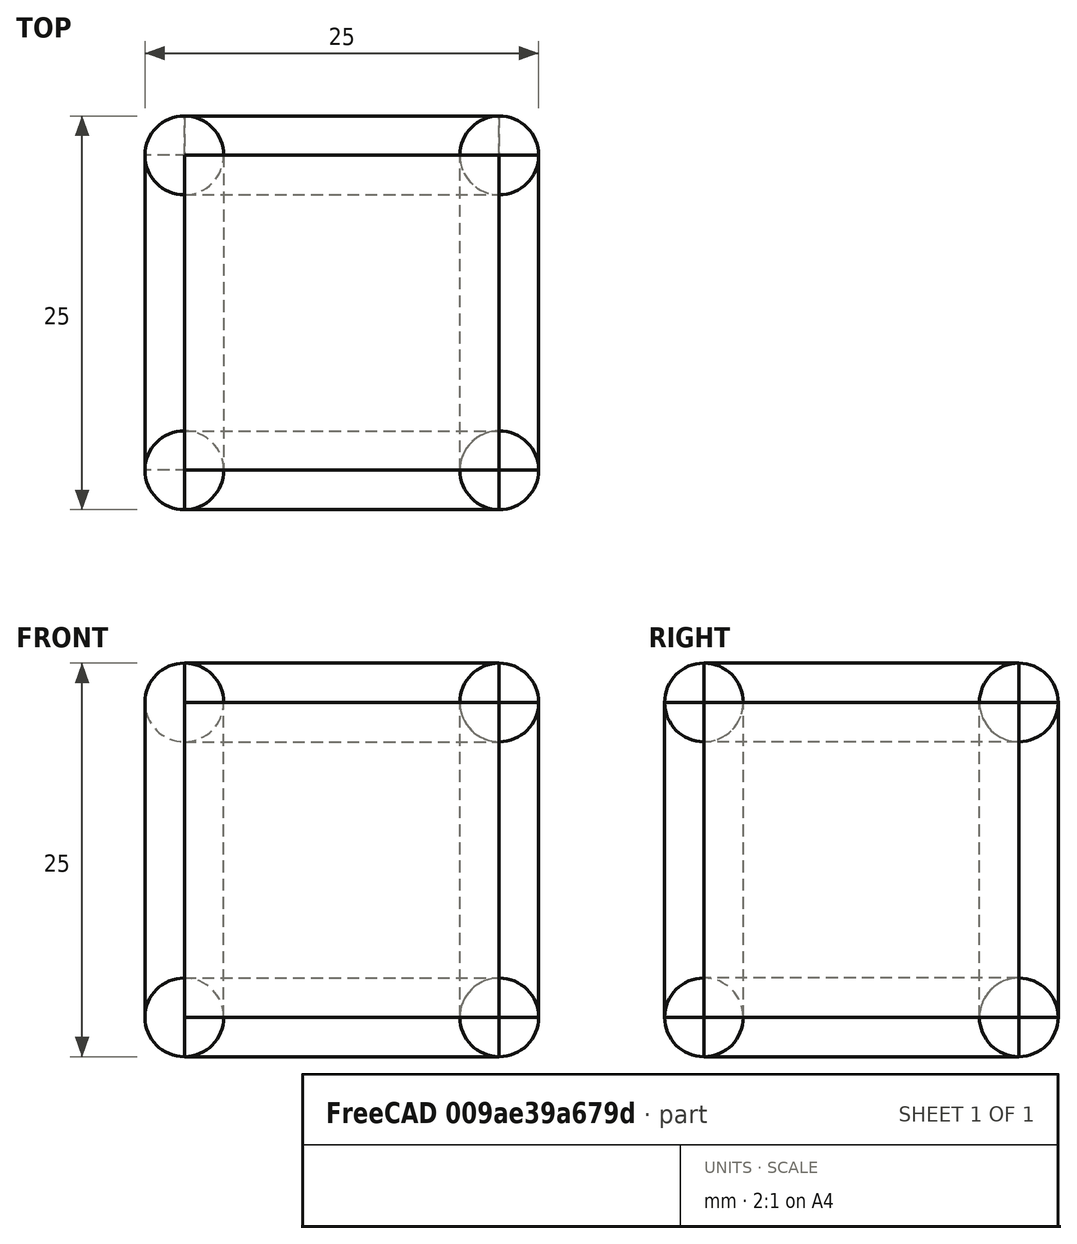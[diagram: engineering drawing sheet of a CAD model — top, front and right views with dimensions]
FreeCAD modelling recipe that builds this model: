
FCSTD DOCUMENT  (FreeCAD 0.16R6706 (Git))
Label: bricks
License: All rights reserved
LicenseURL: http://en.wikipedia.org/wiki/All_rights_reserved
objects: Part::FeaturePython×23, Part::Fuse×2, Part::Part2DObjectPython×2, Part::Sphere×1, Part::Cylinder×1, Part::Box×1, Drawing::FeatureViewPython×1, Drawing::FeaturePage×1
note: 30 computed .brp shape members not serialized (recipe doc carries the construction recipe); baked Part::Feature solids carry a one-line shape summary decoded from their .brp

FEATURE [Part::Sphere] Sphere
  Angle1 = -90
  Angle2 = 90
  Angle3 = 360
  Radius = 2.5
FEATURE [Part::FeaturePython] Clone  label="Clone of Sphere"  # Draft clone (typed FeaturePython)
  Objects = -> [Sphere]
  Placement = pos=(20,0,0) rot=(0,0,1;0rad)
  Scale = (1,1,1)
FEATURE [Part::FeaturePython] Clone001  label="Clone of Sphere001"  # Draft clone (typed FeaturePython)
  Objects = -> [Sphere]
  Placement = pos=(0,20,0) rot=(0,0,1;0rad)
  Scale = (1,1,1)
FEATURE [Part::FeaturePython] Clone002  label="Clone of Sphere002"  # Draft clone (typed FeaturePython)
  Objects = -> [Sphere]
  Placement = pos=(20,20,0) rot=(0,0,1;0rad)
  Scale = (1,1,1)
FEATURE [Part::FeaturePython] Clone003  label="Clone of Clone of Sphere002"  # Draft clone (typed FeaturePython)
  Objects = -> [Clone002]
  Placement = pos=(0,0,20) rot=(0,0,1;0rad)
  Scale = (1,1,1)
FEATURE [Part::FeaturePython] Clone005  label="Clone of Clone of Sphere"  # Draft clone (typed FeaturePython)
  Objects = -> [Clone]
  Placement = pos=(20,0,20) rot=(0,0,1;0rad)
  Scale = (1,1,1)
FEATURE [Part::FeaturePython] Clone004  label="Clone of Clone of Sphere001"  # Draft clone (typed FeaturePython)
  Objects = -> [Clone001]
  Placement = pos=(0,20,20) rot=(0,0,1;0rad)
  Scale = (1,1,1)
FEATURE [Part::FeaturePython] Clone006  label="Clone of Sphere003"  # Draft clone (typed FeaturePython)
  Objects = -> [Sphere]
  Placement = pos=(20,20,20) rot=(0,0,1;0rad)
  Scale = (1,1,1)
FEATURE [Part::Cylinder] Cylinder
  Angle = 360
  Height = 20
  Placement = pos=(0,20,0) rot=(0,0,1;0rad)
  Radius = 2.5
FEATURE [Part::FeaturePython] Clone007  label="Clone of Cylinder"  # Draft clone (typed FeaturePython)
  Objects = -> [Cylinder]
  Scale = (1,1,1)
FEATURE [Part::FeaturePython] Clone008  label="Clone of Cylinder001"  # Draft clone (typed FeaturePython)
  Objects = -> [Cylinder]
  Placement = pos=(20,20,0) rot=(0,0,1;0rad)
  Scale = (1,1,1)
FEATURE [Part::FeaturePython] Clone009  label="Clone of Cylinder002"  # Draft clone (typed FeaturePython)
  Objects = -> [Cylinder]
  Placement = pos=(20,0,0) rot=(0,0,1;0rad)
  Scale = (1,1,1)
FEATURE [Part::FeaturePython] Clone010  label="Clone of Cylinder003"  # Draft clone (typed FeaturePython)
  Objects = -> [Cylinder]
  Placement = pos=(0,20,20) rot=(0,1,0;1.5708rad)
  Scale = (1,1,1)
FEATURE [Part::FeaturePython] Clone011  label="Clone of Clone of Cylinder003"  # Draft clone (typed FeaturePython)
  Objects = -> [Clone010]
  Placement = pos=(0,0,0) rot=(0,1,0;1.5708rad)
  Scale = (1,1,1)
FEATURE [Part::FeaturePython] Clone012  label="Clone of Clone of Cylinder004"  # Draft clone (typed FeaturePython)
  Objects = -> [Clone010]
  Placement = pos=(0,20,0) rot=(0,1,0;1.5708rad)
  Scale = (1,1,1)
FEATURE [Part::FeaturePython] Clone013  label="Clone of Clone of Cylinder005"  # Draft clone (typed FeaturePython)
  Objects = -> [Clone010]
  Placement = pos=(0,0,20) rot=(0,1,0;1.5708rad)
  Scale = (1,1,1)
FEATURE [Part::FeaturePython] Clone014  label="Clone of Cylinder004"  # Draft clone (typed FeaturePython)
  Objects = -> [Cylinder]
  Placement = pos=(0,20,20) rot=(1,0,0;1.5708rad)
  Scale = (1,1,1)
FEATURE [Part::FeaturePython] Clone015  label="Clone of Clone of Cylinder006"  # Draft clone (typed FeaturePython)
  Objects = -> [Clone014]
  Placement = pos=(20,20,0) rot=(1,0,0;1.5708rad)
  Scale = (1,1,1)
FEATURE [Part::FeaturePython] Clone016  label="Clone of Clone of Cylinder007"  # Draft clone (typed FeaturePython)
  Objects = -> [Clone014]
  Placement = pos=(0,20,0) rot=(1,0,0;1.5708rad)
  Scale = (1,1,1)
FEATURE [Part::FeaturePython] Clone017  label="Clone of Clone of Cylinder008"  # Draft clone (typed FeaturePython)
  Objects = -> [Clone014]
  Placement = pos=(20,20,20) rot=(1,0,0;1.5708rad)
  Scale = (1,1,1)
FEATURE [Part::Box] Box001  label="Cube001"
  Height = 20
  Length = 20
  Placement = pos=(0,17.5,0) rot=(0,0,1;0rad)
  Width = 5
FEATURE [Part::FeaturePython] Clone019  label="Clone of Cube002"  # Draft clone (typed FeaturePython)
  Objects = -> [Box001]
  Placement = pos=(0,-2.5,0) rot=(0,0,1;0rad)
  Scale = (1,1,1)
FEATURE [Part::FeaturePython] Clone018  label="Clone of Cube001"  # Draft clone (typed FeaturePython)
  Objects = -> [Box001]
  Placement = pos=(2.5,0,0) rot=(0,0,1;1.5708rad)
  Scale = (1,1,1)
FEATURE [Part::FeaturePython] Clone020  label="Clone of Clone of Cube001"  # Draft clone (typed FeaturePython)
  Objects = -> [Clone018]
  Placement = pos=(22.5,0,0) rot=(0,0,1;1.5708rad)
  Scale = (1,1,1)
FEATURE [Part::FeaturePython] Clone021  label="Clone of Cube003"  # Draft clone (typed FeaturePython)
  Objects = -> [Box001]
  Placement = pos=(0,20,-2.5) rot=(1,0,0;1.5708rad)
  Scale = (1,1,1)
FEATURE [Part::FeaturePython] Clone022  label="Clone of Clone of Cube003"  # Draft clone (typed FeaturePython)
  Objects = -> [Clone021]
  Placement = pos=(0,20,17.5) rot=(1,0,0;1.5708rad)
  Scale = (1,1,1)
FEATURE [Part::Fuse] Fusion
  Base = -> Sphere
  Tool = -> Clone007
FEATURE [Part::Fuse] Fusion001
  Base = -> Clone003
  Tool = -> Fusion
FEATURE [Part::Part2DObjectPython] Line  # Draft 2D object (typed FeaturePython)
  ChamferSize = 0
  Closed = true
  End = (0,200,0)
  FilletRadius = 0
  Length = 200
  MakeFace = true
  Points = (2) [(0,0,0),(0,200,0)]
  Start = (0,0,0)
  Subdivisions = 5
  expr: Subdivisions = 5
  expr: End.x = 0
  expr: End.y = 200
  expr: Length = 200
  expr: Start.y = 0
  expr: Start.x = 0
FEATURE [Part::Part2DObjectPython] Clone2D  label="Clone of Line (2D)"  # Draft 2D object (typed FeaturePython)
  Objects = -> [Line]
  Placement = pos=(0,0,0) rot=(0,0,-1;1.5708rad)
  Scale = (1,1,1)
FEATURE [Drawing::FeatureViewPython] ViewClone  # drawing view (typed FeaturePython)
  Direction = (0,0,0)
  FillStyle = 0
  FontSize = 12
  LineStyle = 0
  LineWidth = 0.35
  Rotation = 0
  Scale = 20
  Source = -> Clone
  Visible = true
  X = 200
  Y = 100
FEATURE [Drawing::FeaturePage] Page
  EditableTexts = AUTHOR NAME | CREATION DATE | SUPERVISOR NAME | CHECK DATE | SCALE | WEIGHT | NUMBER | SHEET | TITLE | SUBTITLE
  Group = -> [ViewClone]
